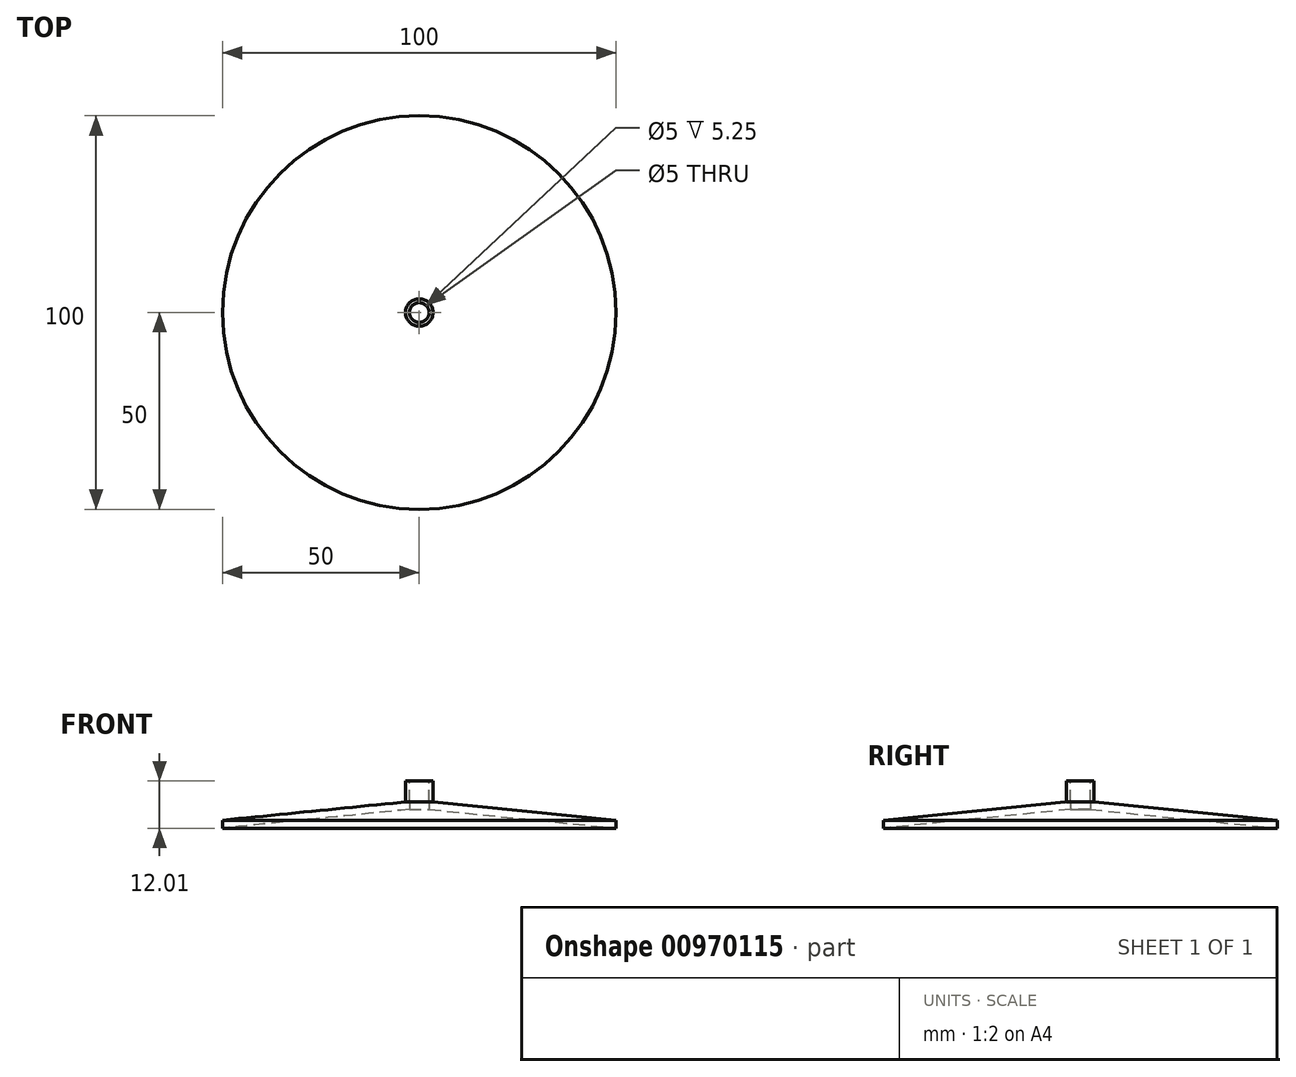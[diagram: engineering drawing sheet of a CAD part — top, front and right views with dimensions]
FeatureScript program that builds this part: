
annotation { "Feature Type Name" : "Feature", "Feature Type Description" : "" }
export const myFeature = defineFeature(function(context is Context, id is Id, definition is map)
    precondition{}
    {
        {
            var Q0;
            Q0=qCreatedBy(makeId("Front.planeOp"),FACE);
            var sketch = newSketch(context, id + "F0", { "sketchPlane" : qUnion([Q0])});
            skLineSegment(sketch, "E0", {"start": v(0, 0) * mm, "end": v(50, 0) * mm});
            skLineSegment(sketch, "E1", {"start": v(50, 0) * mm, "end": v(50, -5) * mm});
            skLineSegment(sketch, "E2", {"start": v(50, -5) * mm, "end": v(0, 0) * mm});
            skLineSegment(sketch, "E3.0", {"start": v(50, -7) * mm, "end": v(0, -2) * mm});
            skLineSegment(sketch, "E4", {"start": v(50, -7) * mm, "end": v(50, -5) * mm});
            skLineSegment(sketch, "E5", {"start": v(0, -2) * mm, "end": v(0, 0) * mm});
            skLineSegment(sketch, "E6.0", {"start": v(2.5, -2.26) * mm, "end": v(2.5, -0.25) * mm});
            skSolve(sketch);
        }
        {
            var Q0;
            {var subQ0=sQuery(id+"F0.wireOp",EDGE,"E4");Q0=makeQuery(id+"F0.imprint","IMPRINT",FACE,{"disambiguationData":[TD([[makeQuery(id+"F0.imprint","IMPRINT",EDGE,{"derivedFrom":subQ0}),1.0]])]});}
            var Q1;
            Q1=sQuery(id+"F0.wireOp",EDGE,"E5");
            revolve(context, id + "F1", {"surfaceOperationType" : NewSurfaceOperationType.NEW, "entities" : qUnion([Q0]), "axis" : qUnion([Q1]), "revolveType" : RevolveType.FULL});
        }
        {
            var Q0;
            Q0=qCreatedBy(makeId("Top.planeOp"),FACE);
            var sketch = newSketch(context, id + "F2", { "sketchPlane" : qUnion([Q0])});
            skCircle(sketch, "E7", {"center": v(0, 0) * mm, "radius": 2.5 * mm});
            skCircle(sketch, "E8", {"center": v(0, 0) * mm, "radius": 3.5 * mm});
            skSolve(sketch);
        }
        {
            var Q0;
            Q0=makeQuery(id+"F2.imprint","IMPRINT",FACE,{"disambiguationData":[TD([[makeQuery(id+"F2.imprint","IMPRINT",EDGE,{"derivedFrom":sQuery(id+"F2.wireOp",EDGE,"E7")}),-1.0]])]});
            var Q1;
            Q1=makeQuery(id+"F1.opRevolve","SWEPT_FACE",FACE,{"disambiguationData":[OSD([sQuery(id+"F0.wireOp",EDGE,"E2")])]});
            extrude(context, id + "F3", {"entities" : qUnion([Q0]), "endBound" : BoundingType.UP_TO_SURFACE, "oppositeDirection" : true, "depth" : 5 * mm, "endBoundEntityFace" : qUnion([Q1]), "offsetDistance" : 10 * mm, "hasSecondDirection" : true, "secondDirectionOppositeDirection" : false, "secondDirectionDepth" : 5 * mm});
        }
    });
